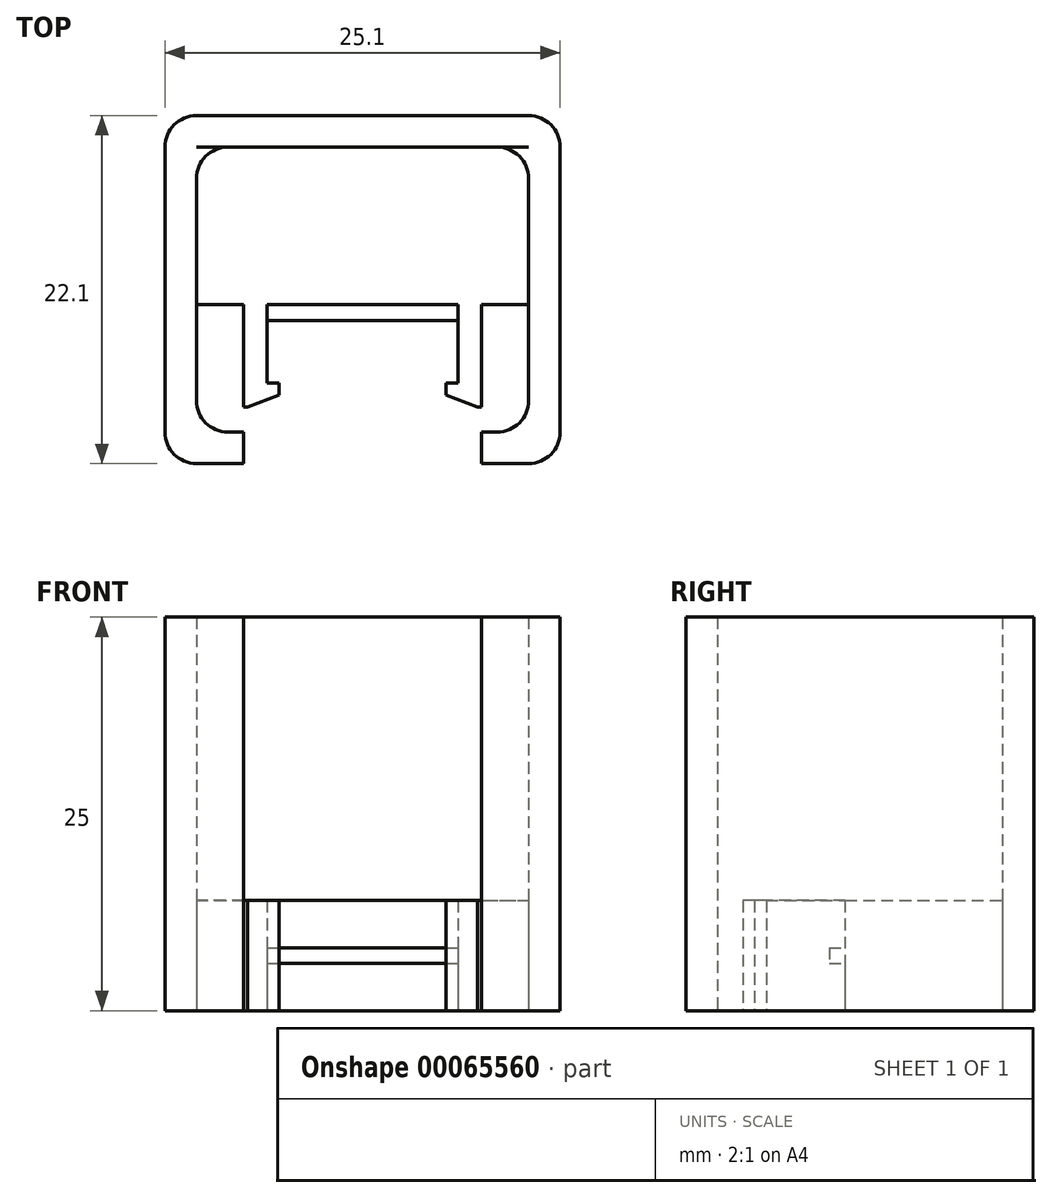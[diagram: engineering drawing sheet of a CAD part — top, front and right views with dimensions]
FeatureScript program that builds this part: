
annotation { "Feature Type Name" : "Feature", "Feature Type Description" : "" }
export const myFeature = defineFeature(function(context is Context, id is Id, definition is map)
    precondition{}
    {
        {
            var Q0;
            Q0=qCreatedBy(makeId("Top.planeOp"),FACE);
            var sketch = newSketch(context, id + "F0", { "sketchPlane" : qUnion([Q0])});
            skLineSegment(sketch, "E0.bottom", {"start": v(6.05, -2.5) * mm, "end": v(-6.05, -2.5) * mm});
            skLineSegment(sketch, "E0.top", {"start": v(6.05, 2.5) * mm, "end": v(-6.05, 2.5) * mm});
            skLineSegment(sketch, "E0.left", {"start": v(6.05, -2.5) * mm, "end": v(6.05, 2.5) * mm});
            skLineSegment(sketch, "E0.right", {"start": v(-6.05, -2.5) * mm, "end": v(-6.05, 2.5) * mm});
            skPoint(sketch, "E0.middle", {"position": v(0, 0) * mm});
            skSolve(sketch);
        }
        {
            var Q0;
            Q0=makeQuery(id+"F0.imprint","IMPRINT",FACE,{"disambiguationData":[TD([[makeQuery(id+"F0.imprint","IMPRINT",EDGE,{"derivedFrom":sQuery(id+"F0.wireOp",EDGE,"E0.bottom")}),-1.0]])]});
            var sketch = newSketch(context, id + "F1", { "sketchPlane" : qUnion([Q0])});
            skLineSegment(sketch, "E1", {"start": v(0, 2.5) * mm, "end": v(0, 4.5) * mm});
            skLineSegment(sketch, "E2", {"start": v(0, 4.5) * mm, "end": v(7.55, 4.5) * mm});
            skLineSegment(sketch, "E3", {"start": v(0, 2.5) * mm, "end": v(6.05, 2.5) * mm});
            skLineSegment(sketch, "E4", {"start": v(6.05, 2.5) * mm, "end": v(6.05, -2.5) * mm});
            skLineSegment(sketch, "E5", {"start": v(7.55, 4.5) * mm, "end": v(7.55, -4) * mm});
            skLineSegment(sketch, "E6", {"start": v(6.05, -2.5) * mm, "end": v(5.3, -2.5) * mm});
            skLineSegment(sketch, "E7", {"start": v(5.3, -2.5) * mm, "end": v(5.3, -3.25) * mm});
            skLineSegment(sketch, "E8", {"start": v(5.3, -3.25) * mm, "end": v(7.3, -4) * mm});
            skLineSegment(sketch, "E9", {"start": v(7.3, -4) * mm, "end": v(7.55, -4) * mm});
            skLineSegment(sketch, "E10.MirrorCS", {"start": v(-7.3, -4) * mm, "end": v(-7.55, -4) * mm});
            skLineSegment(sketch, "E11.MirrorCS", {"start": v(0, 2.5) * mm, "end": v(-6.05, 2.5) * mm});
            skLineSegment(sketch, "E12.MirrorCS", {"start": v(-6.05, 2.5) * mm, "end": v(-6.05, -2.5) * mm});
            skLineSegment(sketch, "E13.MirrorCS", {"start": v(-6.05, -2.5) * mm, "end": v(-5.3, -2.5) * mm});
            skLineSegment(sketch, "E14.MirrorCS", {"start": v(-7.55, 4.5) * mm, "end": v(-7.55, -4) * mm});
            skLineSegment(sketch, "E15.MirrorCS", {"start": v(-5.3, -2.5) * mm, "end": v(-5.3, -3.25) * mm});
            skLineSegment(sketch, "E16.MirrorCS", {"start": v(-5.3, -3.25) * mm, "end": v(-7.3, -4) * mm});
            skLineSegment(sketch, "E17.MirrorCS", {"start": v(0, 4.5) * mm, "end": v(-7.55, 4.5) * mm});
            skSolve(sketch);
        }
        {
            var Q0;
            Q0=makeQuery(id+"F1.imprint","IMPRINT",FACE,{"disambiguationData":[TD([[makeQuery(id+"F1.imprint","IMPRINT",EDGE,{"derivedFrom":sQuery(id+"F1.wireOp",EDGE,"E10.MirrorCS")}),-1.0]])]});
            var Q1;
            Q1=makeQuery(id+"F1.imprint","IMPRINT",FACE,{"disambiguationData":[TD([[makeQuery(id+"F1.imprint","IMPRINT",EDGE,{"derivedFrom":sQuery(id+"F1.wireOp",EDGE,"E2")}),-1.0]])]});
            extrude(context, id + "F2", {"entities" : qUnion([Q0, Q1]), "depth" : 7 * mm});
        }
        {
            var Q0;
            Q0=makeQuery(id+"F2.opExtrude","SWEPT_FACE",FACE,{"disambiguationData":[OSD([sQuery(id+"F1.wireOp",EDGE,"E3"),sQuery(id+"F1.wireOp",EDGE,"E11.MirrorCS")])]});
            var sketch = newSketch(context, id + "F3", { "sketchPlane" : qUnion([Q0])});
            skLineSegment(sketch, "E18.bottom", {"start": v(-6.05, 3) * mm, "end": v(6.05, 3) * mm});
            skLineSegment(sketch, "E18.top", {"start": v(-6.05, 4) * mm, "end": v(6.05, 4) * mm});
            skLineSegment(sketch, "E18.left", {"start": v(-6.05, 4) * mm, "end": v(-6.05, 3) * mm});
            skLineSegment(sketch, "E18.right", {"start": v(6.05, 4) * mm, "end": v(6.05, 3) * mm});
            skSolve(sketch);
        }
        {
            var Q0;
            Q0=makeQuery(id+"F3.imprint","IMPRINT",FACE,{"disambiguationData":[TD([[makeQuery(id+"F3.imprint","IMPRINT",EDGE,{"derivedFrom":sQuery(id+"F3.wireOp",EDGE,"E18.bottom")}),1.0]])]});
            extrude(context, id + "F4", {"entities" : qUnion([Q0]), "operationType" : NewBodyOperationType.ADD, "depth" : 1 * mm});
        }
        {
            var Q0;
            Q0=qCreatedBy(makeId("Top.planeOp"),FACE);
            var sketch = newSketch(context, id + "F5", { "sketchPlane" : qUnion([Q0])});
            skLineSegment(sketch, "E19", {"start": v(-7.55, -4) * mm, "end": v(-7.55, -5.6) * mm});
            skLineSegment(sketch, "E20", {"start": v(-7.55, -5.6) * mm, "end": v(-10.55, -5.6) * mm});
            skLineSegment(sketch, "E21", {"start": v(-10.55, -5.6) * mm, "end": v(-10.55, 12.5) * mm});
            skLineSegment(sketch, "E22", {"start": v(-10.55, 12.5) * mm, "end": v(0, 12.5) * mm});
            skLineSegment(sketch, "E23", {"start": v(0, 12.5) * mm, "end": v(0, 4.5) * mm});
            skLineSegment(sketch, "E24", {"start": v(0, 4.5) * mm, "end": v(-7.55, 4.5) * mm});
            skLineSegment(sketch, "E25", {"start": v(-7.55, 4.5) * mm, "end": v(-7.55, -4) * mm});
            skLineSegment(sketch, "E26.MirrorCS", {"start": v(7.55, -4) * mm, "end": v(7.55, -5.6) * mm});
            skLineSegment(sketch, "E27.MirrorCS", {"start": v(0, 4.5) * mm, "end": v(7.55, 4.5) * mm});
            skLineSegment(sketch, "E28.MirrorCS", {"start": v(7.55, -5.6) * mm, "end": v(10.55, -5.6) * mm});
            skLineSegment(sketch, "E29.MirrorCS", {"start": v(10.55, -5.6) * mm, "end": v(10.55, 12.5) * mm});
            skLineSegment(sketch, "E30.MirrorCS", {"start": v(7.55, 4.5) * mm, "end": v(7.55, -4) * mm});
            skLineSegment(sketch, "E31.MirrorCS", {"start": v(10.55, 12.5) * mm, "end": v(0, 12.5) * mm});
            skLineSegment(sketch, "E32.0", {"start": v(-12.55, 14.5) * mm, "end": v(0, 14.5) * mm});
            skLineSegment(sketch, "E32.1", {"start": v(-12.55, -7.6) * mm, "end": v(-12.55, 14.5) * mm});
            skLineSegment(sketch, "E32.2", {"start": v(-7.55, -7.6) * mm, "end": v(-12.55, -7.6) * mm});
            skLineSegment(sketch, "E33", {"start": v(0, 14.5) * mm, "end": v(0, 12.5) * mm});
            skLineSegment(sketch, "E34", {"start": v(-7.55, -7.6) * mm, "end": v(-7.55, -5.6) * mm});
            skLineSegment(sketch, "E35.MirrorCS", {"start": v(12.55, 14.5) * mm, "end": v(0, 14.5) * mm});
            skLineSegment(sketch, "E36.MirrorCS", {"start": v(12.55, -7.6) * mm, "end": v(12.55, 14.5) * mm});
            skLineSegment(sketch, "E37.MirrorCS", {"start": v(7.55, -7.6) * mm, "end": v(12.55, -7.6) * mm});
            skLineSegment(sketch, "E38.MirrorCS", {"start": v(7.55, -7.6) * mm, "end": v(7.55, -5.6) * mm});
            skLineSegment(sketch, "E39", {"start": v(-7.55, 2.5) * mm, "end": v(-10.55, 2.5) * mm});
            skLineSegment(sketch, "E40.MirrorCS", {"start": v(7.55, 2.5) * mm, "end": v(10.55, 2.5) * mm});
            skSolve(sketch);
        }
        {
            var Q0;
            {var subQ3=sQuery(id+"F5.wireOp",EDGE,"E22");Q0=makeQuery(id+"F5.imprint","IMPRINT",FACE,{"disambiguationData":[TD([[makeQuery(id+"F5.imprint","IMPRINT",EDGE,{"derivedFrom":subQ3}),-1.0]])]});}
            var Q1;
            Q1=makeQuery(id+"F5.imprint","IMPRINT",FACE,{"disambiguationData":[TD([[makeQuery(id+"F5.imprint","IMPRINT",EDGE,{"derivedFrom":sQuery(id+"F5.wireOp",EDGE,"E23")}),1.0]])]});
            extrude(context, id + "F6", {"entities" : qUnion([Q0, Q1]), "operationType" : NewBodyOperationType.ADD, "depth" : 7 * mm});
        }
        {
            var Q0;
            Q0=makeQuery(id+"F5.imprint","IMPRINT",FACE,{"disambiguationData":[TD([[makeQuery(id+"F5.imprint","IMPRINT",EDGE,{"derivedFrom":sQuery(id+"F5.wireOp",EDGE,"E20")}),1.0]])]});
            var Q1;
            Q1=makeQuery(id+"F5.imprint","IMPRINT",FACE,{"disambiguationData":[TD([[makeQuery(id+"F5.imprint","IMPRINT",EDGE,{"derivedFrom":sQuery(id+"F5.wireOp",EDGE,"E28.MirrorCS")}),-1.0]])]});
            extrude(context, id + "F7", {"entities" : qUnion([Q0, Q1]), "depth" : 25 * mm});
        }
        {
            var Q0;
            Q0=makeQuery(id+"F7.opExtrude","SWEPT_EDGE",EDGE,{"disambiguationData":[OSD([sQuery(id+"F5.wireOp",EDGE,"E36.MirrorCS"),sQuery(id+"F5.wireOp",EDGE,"E37.MirrorCS")])]});
            var Q1;
            Q1=makeQuery(id+"F7.opExtrude","SWEPT_EDGE",EDGE,{"disambiguationData":[OSD([sQuery(id+"F5.wireOp",EDGE,"E28.MirrorCS"),sQuery(id+"F5.wireOp",EDGE,"E29.MirrorCS")])]});
            var Q2;
            Q2=makeQuery(id+"F7.opExtrude","SWEPT_EDGE",EDGE,{"disambiguationData":[OSD([sQuery(id+"F5.wireOp",EDGE,"E32.1"),sQuery(id+"F5.wireOp",EDGE,"E32.2")])]});
            var Q3;
            Q3=makeQuery(id+"F7.opExtrude","SWEPT_EDGE",EDGE,{"disambiguationData":[OSD([sQuery(id+"F5.wireOp",EDGE,"E32.0"),sQuery(id+"F5.wireOp",EDGE,"E32.1")])]});
            var Q4;
            Q4=makeQuery(id+"F7.opExtrude","SWEPT_EDGE",EDGE,{"disambiguationData":[OSD([sQuery(id+"F5.wireOp",EDGE,"E35.MirrorCS"),sQuery(id+"F5.wireOp",EDGE,"E36.MirrorCS")])]});
            var Q5;
            Q5=makeQuery(id+"F7.opExtrude","SWEPT_EDGE",EDGE,{"disambiguationData":[OSD([sQuery(id+"F5.wireOp",EDGE,"E20"),sQuery(id+"F5.wireOp",EDGE,"E21")])]});
            var Q6;
            Q6=makeQuery(id+"F7.opExtrude","SWEPT_EDGE",EDGE,{"disambiguationData":[OSD([sQuery(id+"F5.wireOp",EDGE,"E21"),sQuery(id+"F5.wireOp",EDGE,"E22")])]});
            var Q7;
            Q7=makeQuery(id+"F7.opExtrude","SWEPT_EDGE",EDGE,{"disambiguationData":[OSD([sQuery(id+"F5.wireOp",EDGE,"E29.MirrorCS"),sQuery(id+"F5.wireOp",EDGE,"E31.MirrorCS")])]});
            fillet(context, id + "F8", {"entities" : qUnion([Q0, Q1, Q2, Q3, Q4, Q5, Q6, Q7]), "radius" : 2 * mm, "tangentPropagation" : true, "allowEdgeOverflow" : false});
        }
    });
